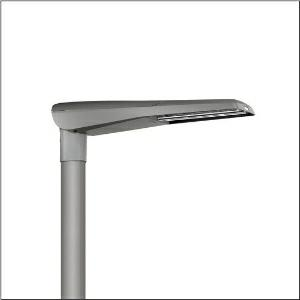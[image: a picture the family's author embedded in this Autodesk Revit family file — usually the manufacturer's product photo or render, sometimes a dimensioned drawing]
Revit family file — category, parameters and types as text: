
# Revit family: streetlight_sl_11_iq_mini___pc-r_5xc2fc1f08he_5d20
name_source: partatom
category: Lighting Fixtures
units: mm (PartAtom-declared; Revit-internal decimal feet)

## family parameters
Cut with Voids When Loaded = No
Host = Face
Light Source = No
Part Type = Normal
Room Calculation Point = No
Round Connector Dimension = Use Diameter
Shared = No

## types (1)
- --- (1 x LED, 5820 lm, 63.6 W, 2200K)
    Apparent Load = 64 VA
    CIE Flux Codes = 37 73 96 100 100
    Color Rendering = 70
    Color Temperature = 2200K
    Default Elevation = 1800 mm
    Description = Streetlight SL 11 iQ mini, mast luminaire, primary light control with 3 zone facetted reflector, of plastic, silver coated, highly specular, primary optical cover: cover, of PMMA, transparent, light distribution: PC-R, light emission: direct distribution, primary light characteristic: asymmetric, right, installation type: post-top, side-entry, lamps: LED, High Power LED, rated values: 7.110lm | 62,2W | 114,3lm/W (begin service life); end service life: 7.110lm | 65,6W; at 50% lumin. flux: 3.555lm | 29,4W | 120,9lm/W, colour temperature: 2200/2700/3000/4000K, colour rendering: CRI > 70, light colour: 722/727/730/740, light setting 1 begin service life: 100% | 7.110lm | 62,2W | 114,3lm/W | 3.000K, light setting 1 end service life: 65,6W, further light settings possible, control: Street-Remote, Auto-Match, Temp-Guard, Lumen-Switch, Night-Set, Smart-Wire, Light-Fading, Desk-Remote (wireless, voltage-free reading and setting of iQ features in the workshop via application-optimized NFC function/RFID function), optimised constant luminous flux control (CLO 2.0), with cable H07RN-F 5x 1.5mm², mains connection: 230..240V, AC, 50/60Hz, connection cable pre-assembled, cable length: 8,5m, luminaire housing, of diecast aluminium, powder-coated, Siteco® metallic grey (DB 702S), please order mast flange separately, inclination adjustable without tools: 0°, 5°, 10°, 15° (post-top) | 0°, -5°, -10°, -15° (side-entry), sealing non-destructively replaceable, multi-level sealing system, length: 736mm, width: 174mm, height: 116mm, mast flange for spigot size: 42mm (side-entry): 5XC10008XM4, 60/48mm (side-entry/post-top): 5XC10108XM2, 76/60mm (side-entry/post-top): 5XC10108XM1, equipment: Power, protection rating (complete): IP66, insulation class (complete): insulation class II (safety insulation), certification: CE, ENEC, ENEC+, VDE, impact resistance: IK10, permissible operating ambient temperature for outdoor applications: -25..+50°C, standard-compliant lighting for roads and squares, Environmental Product Declaration (EPD) tested and certified by an independent institute, packaging unit: 1 piece

Light Distribution: PC-R
    Height = 116 mm
    Lamp = 1 x LED
    Lamp Light Flux = 5820 lm
    Lamp Power = 63.6 W
    Lamp count = 1
    Length = 736 mm
    Luminous efficacy = 92 lm/W
    Manufacturer = Siteco
    ModVariant = No
    Model = 5XC2FC1F08HE
    Number of Poles = 1
    OnlyDefault = Yes
    Power Factor = 1
    Product Name = Streetlight SL 11 iQ mini | PC-R
    Product group = mast luminaire | pylon top
    ProductGroupID = 6100
    Protection Class = Protection class II
    Protection Degree = IP 66
    RLX_Detail_Level = 1
    RLX_Emergency_Light_Flux = 0 lm
    RLX_Emergency_Type = 0
    RLX_Emergency_Type_DB = No
    RlxData = <blob elided: 57377 chars, md5=76fe3b07>
    Socket = socket
    Standby Power = 0 W
    System Light Flux = 5820 lm
    System Power = 64 W
    Type Comments = individual setting: luminous flux: 100 % | dim-lin: 254 | 866 mA
    Type Image = l_1003508.jpg
    URL = http://relux.com
    VarID = @adj_032180
    Voltage = 0 V
    Weight = 0.00 kg
    Width = 174 mm

## geometry (parser evidence)
native form markers: Blend x4, Sweep x11
no freeform markers — native parametric forms only
